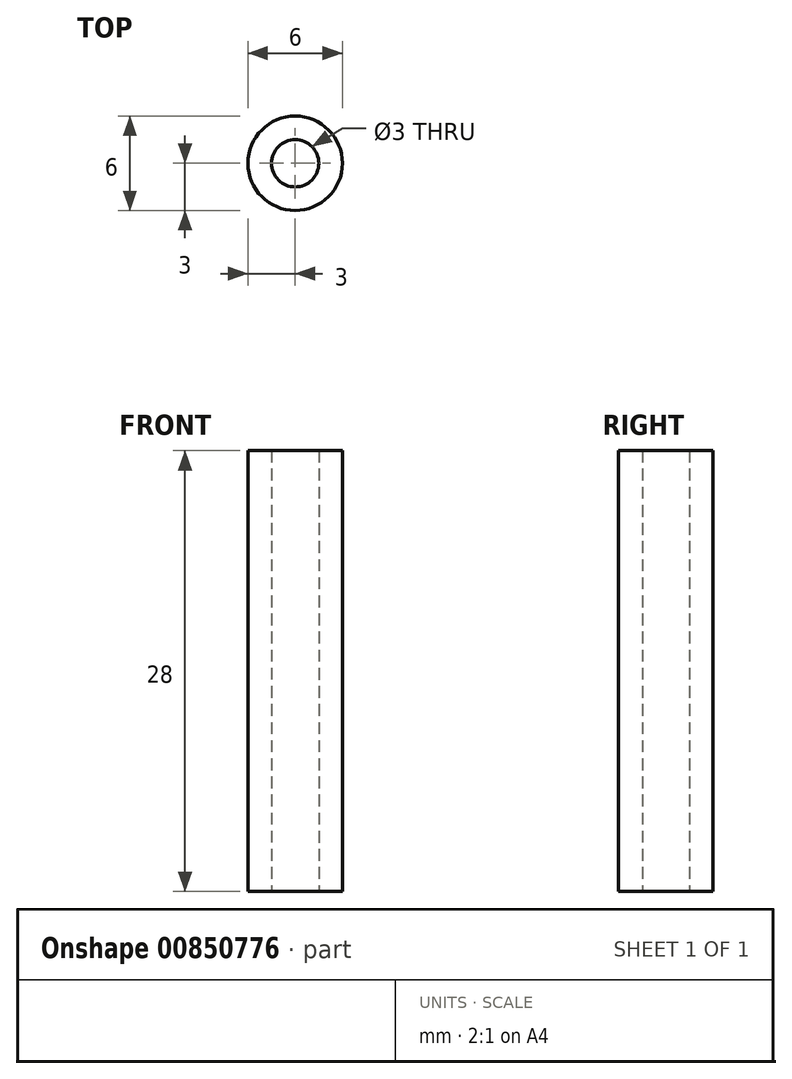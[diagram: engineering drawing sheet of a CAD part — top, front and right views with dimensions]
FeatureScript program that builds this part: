
annotation { "Feature Type Name" : "Feature", "Feature Type Description" : "" }
export const myFeature = defineFeature(function(context is Context, id is Id, definition is map)
    precondition{}
    {
        {
            var Q0;
            Q0=qCreatedBy(makeId("Top.planeOp"),FACE);
            var sketch = newSketch(context, id + "F0", { "sketchPlane" : qUnion([Q0])});
            skCircle(sketch, "E0", {"center": v(0, 0) * mm, "radius": 1.5 * mm});
            skCircle(sketch, "E1", {"center": v(0, 0) * mm, "radius": 3 * mm});
            skSolve(sketch);
        }
        {
            var Q0;
            Q0=qSketchRegion(id+"F0",true);
            extrude(context, id + "F1", {"entities" : qUnion([Q0]), "depth" : 28 * mm, "offsetDistance" : 25 * mm});
        }
    });
